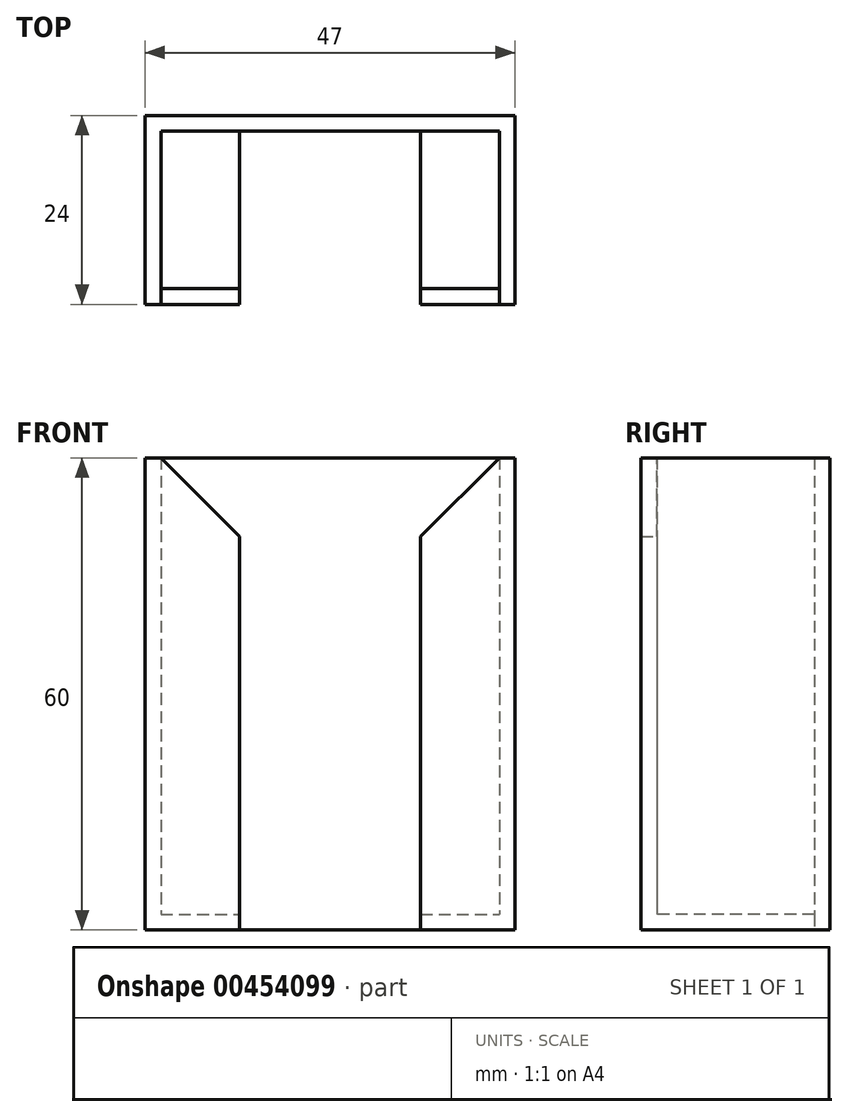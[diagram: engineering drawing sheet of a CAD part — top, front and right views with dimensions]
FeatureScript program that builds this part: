
annotation { "Feature Type Name" : "Feature", "Feature Type Description" : "" }
export const myFeature = defineFeature(function(context is Context, id is Id, definition is map)
    precondition{}
    {
        {
            var Q0;
            Q0=qCreatedBy(makeId("Top.planeOp"),FACE);
            var sketch = newSketch(context, id + "F0", { "sketchPlane" : qUnion([Q0])});
            skLineSegment(sketch, "E0.bottom", {"start": v(-19.53, 9.04) * mm, "end": v(23.47, 9.04) * mm});
            skLineSegment(sketch, "E0.top", {"start": v(-19.53, -10.96) * mm, "end": v(23.47, -10.96) * mm});
            skLineSegment(sketch, "E0.left", {"start": v(-19.53, 9.04) * mm, "end": v(-19.53, -10.96) * mm});
            skLineSegment(sketch, "E0.right", {"start": v(23.47, 9.04) * mm, "end": v(23.47, -10.96) * mm});
            skLineSegment(sketch, "E1.bottom", {"start": v(-21.53, 11.04) * mm, "end": v(25.47, 11.04) * mm});
            skLineSegment(sketch, "E1.top", {"start": v(-21.53, -12.96) * mm, "end": v(25.47, -12.96) * mm});
            skLineSegment(sketch, "E1.left", {"start": v(-21.53, 11.04) * mm, "end": v(-21.53, -12.96) * mm});
            skLineSegment(sketch, "E1.right", {"start": v(25.47, 11.04) * mm, "end": v(25.47, -12.96) * mm});
            skLineSegment(sketch, "E2", {"start": v(13.47, -10.96) * mm, "end": v(13.47, -12.96) * mm});
            skLineSegment(sketch, "E3", {"start": v(-9.53, -10.96) * mm, "end": v(-9.53, -12.96) * mm});
            skLineSegment(sketch, "E4", {"start": v(-9.53, -10.96) * mm, "end": v(-9.53, 9.04) * mm});
            skLineSegment(sketch, "E5", {"start": v(13.47, -10.96) * mm, "end": v(13.47, 9.04) * mm});
            skSolve(sketch);
        }
        {
            var Q0;
            {var subQ4=sQuery(id+"F0.wireOp",EDGE,"E0.left");Q0=makeQuery(id+"F0.imprint","IMPRINT",FACE,{"disambiguationData":[TD([[makeQuery(id+"F0.imprint","IMPRINT",EDGE,{"derivedFrom":subQ4}),-1.0]])]});}
            extrude(context, id + "F1", {"entities" : qUnion([Q0]), "depth" : 60 * mm});
        }
        {
            var Q0;
            {var subQ0=sQuery(id+"F0.wireOp",EDGE,"E0.left");Q0=makeQuery(id+"F0.imprint","IMPRINT",FACE,{"disambiguationData":[TD([[makeQuery(id+"F0.imprint","IMPRINT",EDGE,{"derivedFrom":subQ0}),1.0]])]});}
            var Q1;
            {var subQ0=sQuery(id+"F0.wireOp",EDGE,"E0.right");Q1=makeQuery(id+"F0.imprint","IMPRINT",FACE,{"disambiguationData":[TD([[makeQuery(id+"F0.imprint","IMPRINT",EDGE,{"derivedFrom":subQ0}),-1.0]])]});}
            extrude(context, id + "F2", {"entities" : qUnion([Q0, Q1]), "operationType" : NewBodyOperationType.ADD, "depth" : 2 * mm});
        }
        {
            var Q0;
            Q0=makeQuery(id+"F1.opExtrude","CAP_EDGE",EDGE,{"disambiguationData":[OSD([sQuery(id+"F0.wireOp",EDGE,"E3")])],"isStart":false});
            var Q1;
            Q1=makeQuery(id+"F1.opExtrude","CAP_EDGE",EDGE,{"disambiguationData":[OSD([sQuery(id+"F0.wireOp",EDGE,"E2")])],"isStart":false});
            chamfer(context, id + "F3", {"entities" : qUnion([Q0, Q1]), "width" : 10 * mm, "tangentPropagation" : true});
        }
    });
